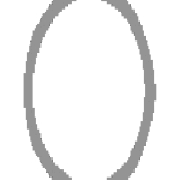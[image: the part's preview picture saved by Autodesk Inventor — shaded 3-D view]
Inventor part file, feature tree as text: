
AUTODESK INVENTOR PART (.ipt)
format: ipt  version: 2021 (Build 250183000, 183)  size: 111,616 bytes
history: native  units: in
note: dims shown in document units (in); Inventor stores cm internally (conversion verified against a paired STEP export)
features: other x4, sketch x3, plane x1
ambient origin geometry x8: Origin, YZ Plane, XZ Plane, XY Plane, X Axis, Y Axis, Z Axis, Center Point
bodies: Solid1 (feature_tree), Body (feature_tree)
feature tree (8):
  other  "Driven Length"
  other  "Frame Generator"
  other  "Start Plane"
  other  "End Plane"
  sketch  "Sketch"  dims[d2=6.0828in d4=-0.0in d5=6.0828in d6=0.12in d7=0.0in d8=90.0deg d9=6.0828in]
  sketch  "Sketch2"  dims[d0=1.0in]
  plane  "Work Plane3"
  sketch  "Sketch3"  dims[d1=0.065in]
